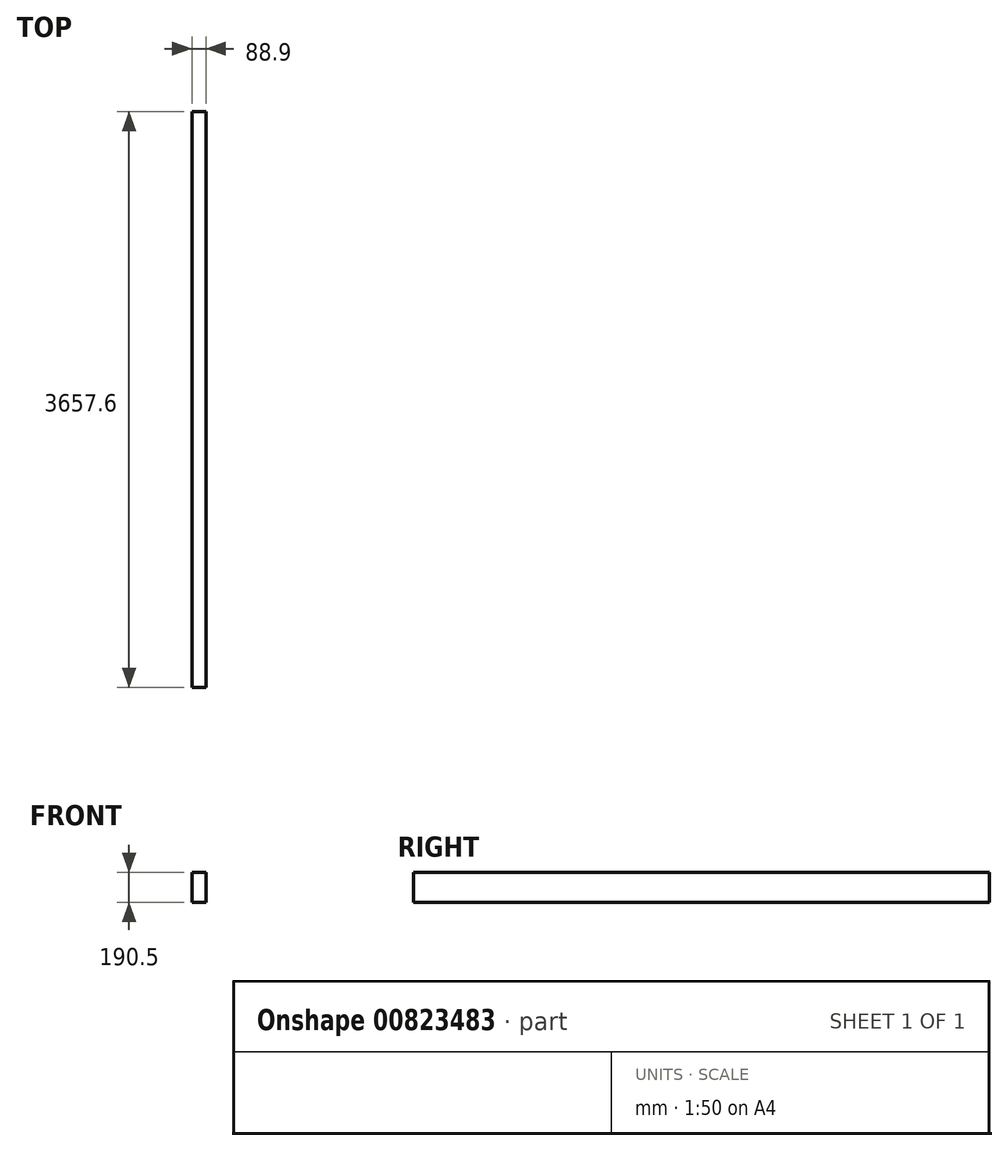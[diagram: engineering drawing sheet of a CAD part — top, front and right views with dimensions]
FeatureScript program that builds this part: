
annotation { "Feature Type Name" : "Feature", "Feature Type Description" : "" }
export const myFeature = defineFeature(function(context is Context, id is Id, definition is map)
    precondition{}
    {
        {
            var Q0;
            Q0=qCreatedBy(makeId("Front.planeOp"),FACE);
            var sketch = newSketch(context, id + "F0", { "sketchPlane" : qUnion([Q0])});
            skLineSegment(sketch, "E0.bottom", {"start": v(0, 0) * mm, "end": v(88.9, 0) * mm});
            skLineSegment(sketch, "E0.top", {"start": v(0, 190.5) * mm, "end": v(88.9, 190.5) * mm});
            skLineSegment(sketch, "E0.left", {"start": v(0, 0) * mm, "end": v(0, 190.5) * mm});
            skLineSegment(sketch, "E0.right", {"start": v(88.9, 0) * mm, "end": v(88.9, 190.5) * mm});
            skSolve(sketch);
        }
        {
            var Q0;
            Q0 = qSketchRegion(id + "F0", true);
            extrude(context, id + "F1", {"entities" : qUnion([Q0]), "depth" : 3657.6 * mm, "offsetDistance" : 25.4 * mm});
        }
    });
